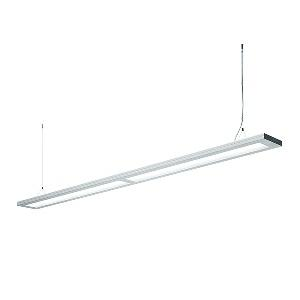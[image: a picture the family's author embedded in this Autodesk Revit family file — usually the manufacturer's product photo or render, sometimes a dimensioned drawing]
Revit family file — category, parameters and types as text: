
# Revit family: lavigo_-_dpp_13000_840_d_g2_00800703_4390
name_source: partatom
category: Lighting Fixtures
units: mm (PartAtom-declared; Revit-internal decimal feet)

## family parameters
Cut with Voids When Loaded = No
Host = Face
Light Source = No
Part Type = Normal
Room Calculation Point = No
Round Connector Dimension = Use Diameter
Shared = No

## types (1)
- LAVIGO - DPP 13000/840/D/G2 (1 x LED, 13800 lm, 4000K)
    Apparent Load = 97 VA
    Approval mark = CE
    CIE Flux Codes = 60 87 97 25 100
    Color Rendering = 80-89
    Color Temperature = 4000K
    Control Gear = Electronic ballast
    Default Elevation = 1800 mm
    Description = DPP 13000/840/D/G2|Suspended luminaire|light source: LED|connected load: 220-240 V, 50/60 Hz|Power consumption: approx. 97 W|standby: approx. 0,50|luminous flux: 13800 lm|luminous efficacy: 142 lm/W|light distribution: Direct/indirect|direct ratio: approx. 25 %|colour temperature: Cold white, ca. 4000 K|color rendering index (CRI): >= 80|chromaticity tolerance:  3 SDCM|System of protection: IP 20|technology: Continuously dimmable|luminaire body|material: Steel/plastic|surface: Powder coatet|colour: White|lamp cover: Polycarbonate (PC), Clear|mains lead: 1.00 m With free stranded wires|Fastening: Steel cable 0.3 - 0.7 m|decorative contrast side parts: Flint grey|glare control: Prism aperture|luminance(L65): <= 2700 cd/m|unified glare rating(4H 8H): <=  16|special features: Canopy colour (pure white), Cradle to Cradle Certified TM, DALI - dimming via digital rotary dimmer, DALI Load 2x, TouchDIM - dimming via standard switch, Direct light component with edge light and light-guide technology for homogenous light exit, Integration into DALI light management systems, Flicker-free|
    Frequency = 50 Hz
    Height = 36 mm
    Lamp = 1 x LED
    Lamp Light Flux = 13800 lm
    Lamp count = 1
    Length = 2430 mm
    Luminous efficacy = 142 lm/W
    Manufacturer = Waldmann
    ModVariant = No
    Model = 00800703
    Mounting Place = Ceiling
    Mounting Type = Pendant
    Number of Poles = 1
    OnlyDefault = Yes
    Power Factor = 1
    Product Name = LAVIGO - DPP 13000/840/D/G2
    Product group = Suspended luminaire
    ProductGroupID = 9
    Protection Class = Protection class I
    Protection Degree = IP 20
    RLX_Detail_Level = 1
    RLX_Emergency_Light_Flux = 0 lm
    RLX_Emergency_Type = 0
    RLX_Emergency_Type_DB = No
    RlxData = <blob elided: 25489 chars, md5=2a772c12>
    Socket = socket
    Standby Power = 0 W
    System Light Flux = 13800 lm
    System Power = 97 W
    Type Comments = Product without accessories
    Type Image = 121742000-00681438.jpg
    URL = http://relux.com
    VarID = ---
    Voltage = 230 V
    Voltage Range = 220-240 V
    Weight = 0.00 kg
    Width = 200 mm  [stored 0.656168 ft]

note: [stored X ft] marks values corroborated as IEEE doubles in the binary element streams (Revit-internal decimal feet)

## geometry (parser evidence)
native form markers: Blend x4, Sweep x14
no freeform markers — native parametric forms only
